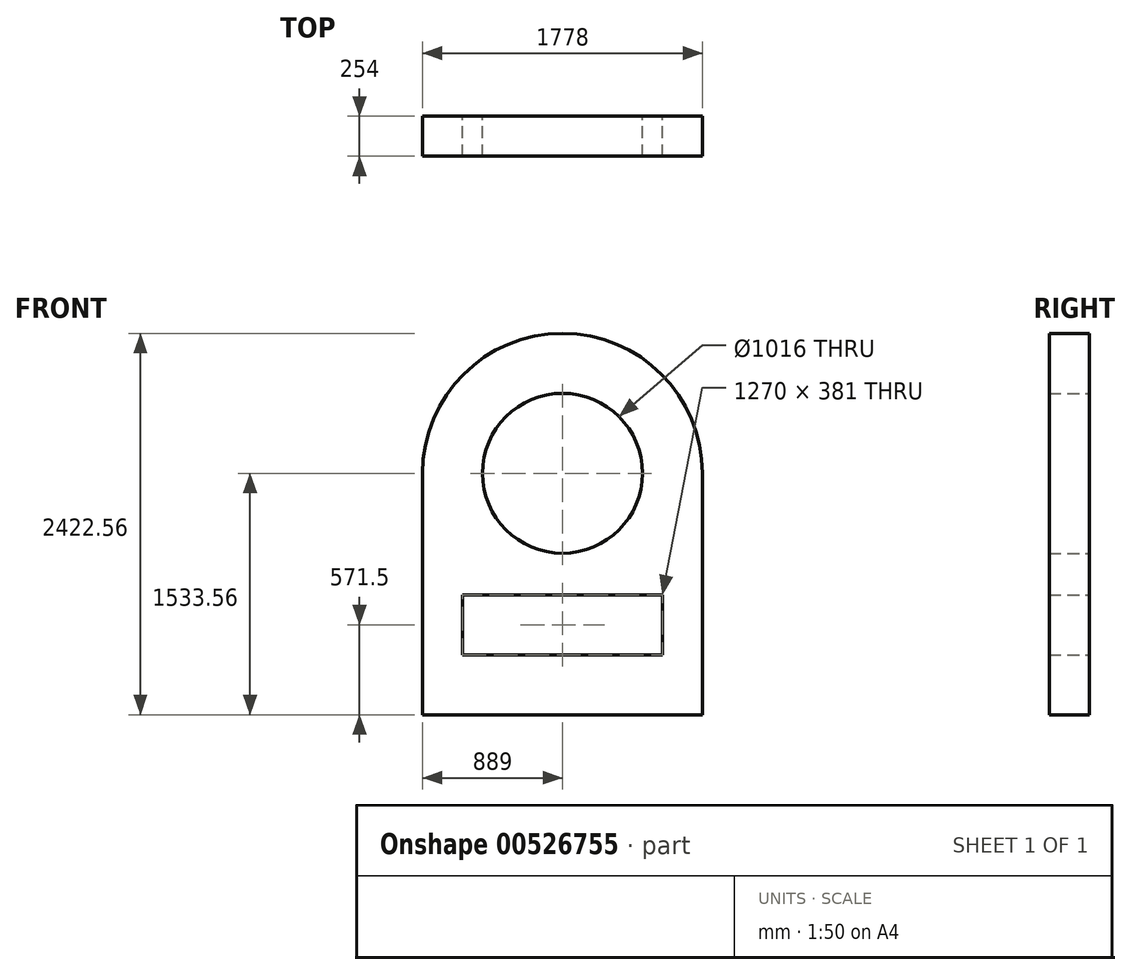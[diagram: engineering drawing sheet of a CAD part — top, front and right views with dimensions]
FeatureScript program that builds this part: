
annotation { "Feature Type Name" : "Feature", "Feature Type Description" : "" }
export const myFeature = defineFeature(function(context is Context, id is Id, definition is map)
    precondition{}
    {
        {
            var Q0;
            Q0=qCreatedBy(makeId("Front.planeOp"),FACE);
            var sketch = newSketch(context, id + "F0", { "sketchPlane" : qUnion([Q0])});
            skLineSegment(sketch, "E0", {"start": v(0, 0) * mm, "end": v(1778, 0) * mm});
            skLineSegment(sketch, "E1", {"start": v(0, 0) * mm, "end": v(0, 1524) * mm});
            skLineSegment(sketch, "E2", {"start": v(1778, 0) * mm, "end": v(1778, 1524) * mm});
            skArc(sketch, "E3", {"start": v(1778, 1533.56) * mm, "mid": v(889, 2422.56) * mm, "end": v(0, 1533.56) * mm});
            skLineSegment(sketch, "E4", {"start": v(0, 1524) * mm, "end": v(0, 1533.56) * mm});
            skLineSegment(sketch, "E5", {"start": v(1778, 1524) * mm, "end": v(1778, 1533.56) * mm});
            skLineSegment(sketch, "E6", {"start": v(254, 762) * mm, "end": v(1524, 762) * mm});
            skLineSegment(sketch, "E7", {"start": v(1524, 762) * mm, "end": v(1524, 381) * mm});
            skLineSegment(sketch, "E8", {"start": v(1524, 381) * mm, "end": v(254, 381) * mm});
            skLineSegment(sketch, "E9", {"start": v(254, 762) * mm, "end": v(254, 381) * mm});
            skCircle(sketch, "E10", {"center": v(889, 1533.56) * mm, "radius": 508 * mm});
            skSolve(sketch);
        }
        {
            var Q0;
            Q0 = qSketchRegion(id + "F0", true);
            extrude(context, id + "F1", {"entities" : qUnion([Q0]), "depth" : 254 * mm, "offsetDistance" : 25.4 * mm});
        }
    });
